# Revit family: ARKOSLIGHT_Standup
name_source: partatom
category: Lighting Fixtures
units: mm (PartAtom-declared; Revit-internal decimal feet)

## family parameters
Always vertical = Yes
Cut with Voids When Loaded = No
Light Source = No
OmniClass Number = 23.80.70.00
OmniClass Title = Lighting
Part Type = Normal
Room Calculation Point = No
Round Connector Dimension = Use Diameter
Shared = No
Work Plane-Based = No

## types (1)
- ARKOSLIGHT_Standup
    ARKOSLIGHT_Apparent Load = 27 VA
    ARKOSLIGHT_Beam Angle = 105.00°
    ARKOSLIGHT_Body Color = ARKOSLIGHT_Textured black
    ARKOSLIGHT_CCT = 2700 K
    ARKOSLIGHT_CRI = CRI>90
    ARKOSLIGHT_Color = Textured Black
    ARKOSLIGHT_Dimming = ON BOARD
    ARKOSLIGHT_Efficiency = 66%
    ARKOSLIGHT_Fixture Type = WALL, FLOOR & PORTABLE
    ARKOSLIGHT_IES = A4940000 NT STANDUP 2700K.ies
    ARKOSLIGHT_IP = 20
    ARKOSLIGHT_Luminous flux = 4210 lm
    ARKOSLIGHT_Model = STANDUP
    ARKOSLIGHT_Reference = A4940000NT
    ARKOSLIGHT_Series = STANDUP
    ARKOSLIGHT_Wattage = 34 W
    Apparent Load = 27 VA
    IES = IES : A4940000NT - STANDUP 2700K NT
    Manufacturer = ARKOSLIGHT
    Model = ARKOSLIGHT_Model
    URL = https://www.arkoslight.com

## geometry (parser evidence)
native form markers: Sweep x4
no freeform markers — native parametric forms only
